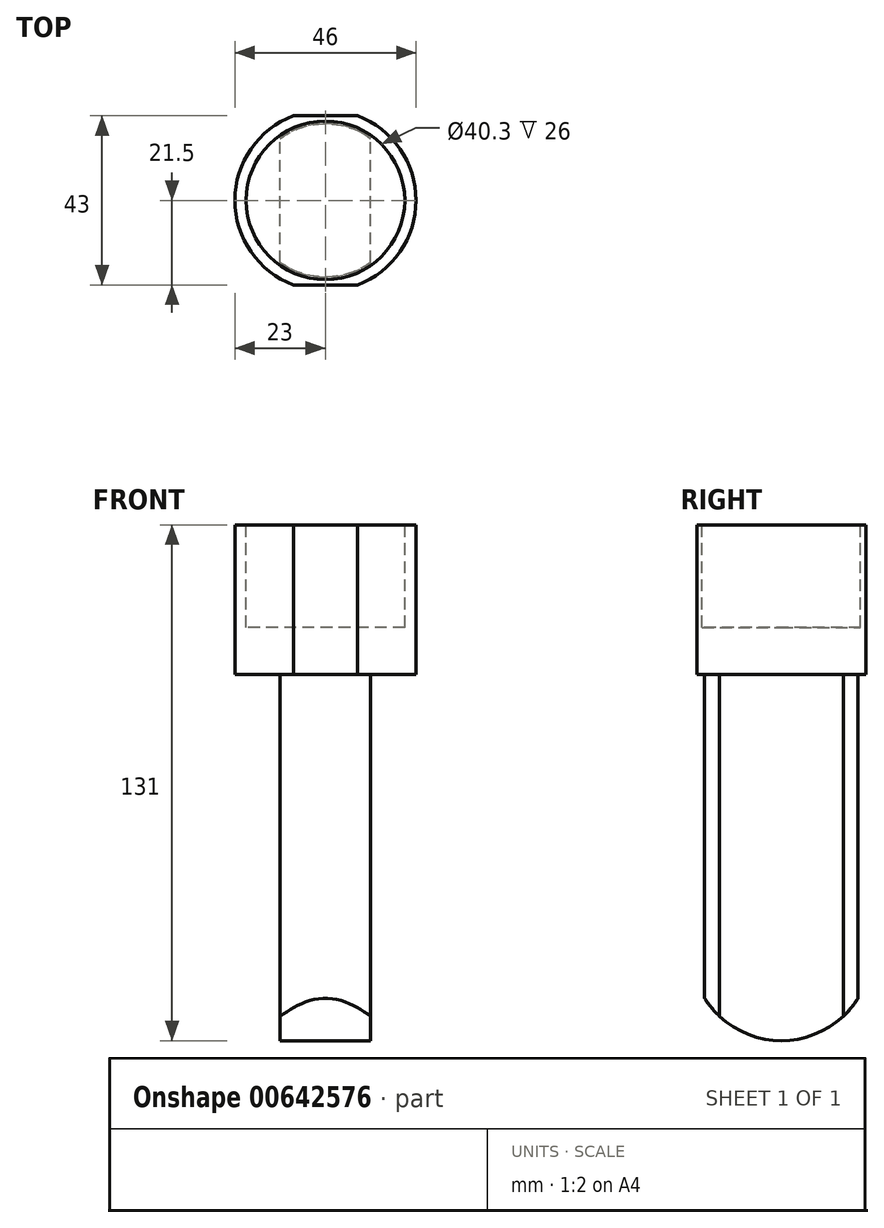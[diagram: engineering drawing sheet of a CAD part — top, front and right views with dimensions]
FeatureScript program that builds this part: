
annotation { "Feature Type Name" : "Feature", "Feature Type Description" : "" }
export const myFeature = defineFeature(function(context is Context, id is Id, definition is map)
    precondition{}
    {
        {
            var Q0;
            Q0=qCreatedBy(makeId("Top.planeOp"),FACE);
            var sketch = newSketch(context, id + "F0", { "sketchPlane" : qUnion([Q0])});
            skArc(sketch, "E0", {"start": v(8.17, -21.5) * mm, "mid": v(23, 0) * mm, "end": v(8.17, 21.5) * mm});
            skLineSegment(sketch, "E1", {"start": v(-8.17, -21.5) * mm, "end": v(8.17, -21.5) * mm});
            skLineSegment(sketch, "E2.MirrorCS", {"start": v(-8.17, 21.5) * mm, "end": v(8.17, 21.5) * mm});
            skArc(sketch, "E3.trimOffspring", {"start": v(-8.17, 21.5) * mm, "mid": v(-23, 0) * mm, "end": v(-8.17, -21.5) * mm});
            skSolve(sketch);
        }
        {
            var Q0;
            Q0 = qSketchRegion(id + "F0", true);
            extrude(context, id + "F1", {"entities" : qUnion([Q0]), "depth" : 38 * mm, "offsetDistance" : 25 * mm});
        }
        {
            var Q0;
            Q0=makeQuery(id+"F1.opExtrude","CAP_FACE",FACE,{"disambiguationData":[OSD([sQuery(id+"F0.wireOp",EDGE,"E0"),sQuery(id+"F0.wireOp",EDGE,"E1"),sQuery(id+"F0.wireOp",EDGE,"E2.MirrorCS"),sQuery(id+"F0.wireOp",EDGE,"E3.trimOffspring")])],"isStart":false});
            var sketch = newSketch(context, id + "F2", { "sketchPlane" : qUnion([Q0])});
            skCircle(sketch, "E4", {"center": v(0, 0) * mm, "radius": 20.15 * mm});
            skSolve(sketch);
        }
        {
            var Q0;
            Q0=makeQuery(id+"F2.imprint","IMPRINT",FACE,{"disambiguationData":[TD([[makeQuery(id+"F2.imprint","IMPRINT",EDGE,{"derivedFrom":sQuery(id+"F2.wireOp",EDGE,"E4")}),1.0]])]});
            extrude(context, id + "F3", {"entities" : qUnion([Q0]), "operationType" : NewBodyOperationType.REMOVE, "oppositeDirection" : true, "depth" : 26 * mm, "offsetDistance" : 25 * mm});
        }
        {
            var Q0;
            Q0=makeQuery(id+"F1.opExtrude","CAP_FACE",FACE,{"disambiguationData":[OSD([sQuery(id+"F0.wireOp",EDGE,"E0"),sQuery(id+"F0.wireOp",EDGE,"E1"),sQuery(id+"F0.wireOp",EDGE,"E2.MirrorCS"),sQuery(id+"F0.wireOp",EDGE,"E3.trimOffspring")])],"isStart":true});
            var sketch = newSketch(context, id + "F4", { "sketchPlane" : qUnion([Q0])});
            skArc(sketch, "E5", {"start": v(-11.5, -15.75) * mm, "mid": v(0, -19.5) * mm, "end": v(11.5, -15.75) * mm});
            skLineSegment(sketch, "E6", {"start": v(-11.5, 15.75) * mm, "end": v(-11.5, -15.75) * mm});
            skLineSegment(sketch, "E7.MirrorCS", {"start": v(11.5, 15.75) * mm, "end": v(11.5, -15.75) * mm});
            skArc(sketch, "E8.trimOffspring", {"start": v(11.5, 15.75) * mm, "mid": v(0, 19.5) * mm, "end": v(-11.5, 15.75) * mm});
            skSolve(sketch);
        }
        {
            var Q0;
            Q0=makeQuery(id+"F4.imprint","IMPRINT",FACE,{"disambiguationData":[TD([[makeQuery(id+"F4.imprint","IMPRINT",EDGE,{"derivedFrom":sQuery(id+"F4.wireOp",EDGE,"E5")}),1.0]])]});
            extrude(context, id + "F5", {"entities" : qUnion([Q0]), "operationType" : NewBodyOperationType.ADD, "depth" : 93 * mm, "offsetDistance" : 25 * mm});
        }
        {
            var Q0;
            Q0=makeQuery(id+"F5.opExtrude","SWEPT_FACE",FACE,{"disambiguationData":[OSD([sQuery(id+"F4.wireOp",EDGE,"E7.MirrorCS")])]});
            var sketch = newSketch(context, id + "F6", { "sketchPlane" : qUnion([Q0])});
            skArc(sketch, "E9", {"start": v(-23, -70) * mm, "mid": v(0, -93) * mm, "end": v(23, -70) * mm});
            skLineSegment(sketch, "E10", {"start": v(-23, -70) * mm, "end": v(23, -70) * mm});
            skLineSegment(sketch, "E11", {"start": v(-23, -70) * mm, "end": v(-31.36, -101.49) * mm});
            skLineSegment(sketch, "E12", {"start": v(-31.36, -101.49) * mm, "end": v(37.3, -101.49) * mm});
            skLineSegment(sketch, "E13", {"start": v(37.3, -101.49) * mm, "end": v(23, -70) * mm});
            skSolve(sketch);
        }
        {
            var Q0;
            {var subQ0=sQuery(id+"F6.wireOp",EDGE,"E11");Q0=makeQuery(id+"F6.imprint","IMPRINT",FACE,{"disambiguationData":[TD([[makeQuery(id+"F6.imprint","IMPRINT",EDGE,{"derivedFrom":subQ0}),1.0]])]});}
            var Q1;
            {var subQ0=sQuery(id+"F6.wireOp",EDGE,"E9");var subQ1=sQuery(id+"F4.wireOp",EDGE,"E7.MirrorCS");var subQ2=makeQuery(id+"F5.opExtrude","CAP_EDGE",EDGE,{"disambiguationData":[OSD([subQ1])],"isStart":false});var subQ3=makeQuery(id+"F6.imprint","INTERSECT",VERTEX,{"derivedFrom":[subQ2,subQ0]});Q1=makeQuery(id+"F6.imprint","IMPRINT",FACE,{"disambiguationData":[TD([[makeQuery(id+"F6.imprint","IMPRINT",EDGE,{"disambiguationData":[TD([[subQ3,-1.0]])],"derivedFrom":subQ0}),-1.0]])]});}
            var Q2;
            {var subQ0=sQuery(id+"F6.wireOp",EDGE,"E9");var subQ1=sQuery(id+"F4.wireOp",EDGE,"E7.MirrorCS");var subQ4=makeQuery(id+"F5.opExtrude","CAP_EDGE",EDGE,{"disambiguationData":[OSD([subQ1])],"isStart":false});var subQ5=makeQuery(id+"F6.imprint","INTERSECT",VERTEX,{"derivedFrom":[subQ4,subQ0]});Q2=makeQuery(id+"F6.imprint","IMPRINT",FACE,{"disambiguationData":[TD([[makeQuery(id+"F6.imprint","IMPRINT",EDGE,{"disambiguationData":[TD([[subQ5,1.0]])],"derivedFrom":subQ0}),-1.0]])]});}
            extrude(context, id + "F7", {"entities" : qUnion([Q0, Q1, Q2]), "operationType" : NewBodyOperationType.REMOVE, "endBound" : BoundingType.THROUGH_ALL, "oppositeDirection" : true, "depth" : 25 * mm, "offsetDistance" : 25 * mm});
        }
    });
